# Revit family: Window-Casement-Pella-Architect_Series-Fixed
name_source: partatom
category: Windows
revit_build: Autodesk Revit Architecture 2013 (Build: 20130531_2115(x64)
units: mm (PartAtom-declared; Revit-internal decimal feet)

## types (88) — shared parameters
Analytic Construction = <None>
Architectural Data Sheet = To be determined
Architectural Design Manual = www.pellaadm.com
Construction Type = -
Cross Grille Pattern = No
Custom Grille Pattern = No
Custom Horizontal Lites = 2
Custom Vertical Lites = 3
Default Sill Height = 2' - 7 1/2"
Description = Casement - Fixed Unit
Egress Window = No
Energy Efficiency = http://www.pella.com
Environmental Commitment = http://www.pella.com
Ext Finish = Aluminum - Pella - Brown
Glazing Finish = Glass - Pella - Clear Insulating Glass
Glazing Thickness = 0' - 0 5/8"
Grille Visibility = Yes
Heat Transfer Coefficient (U) = 0.1000 BTU/(h·ft²·°F)
Int Finish = Wood - Pella - Pine
Manufacturer = Pella Windows & Doors
Operation = Fixed
Prairie Grille Pattern = No
Product Documentation Link = http://media.pella.com
Product Name = Architect Series Casement Window
Product Page URL = http://www.pella.com
Series = Architect Series - Aluminum-Clad Wood
Size Constraints = Window Sizing constraints available in 6.35 mm increments
Thermal Resistance (R) = 10.0000 (h·ft²·°F)/BTU
Top Row Grille Pattern = No
Traditional Grille Pattern = Yes
URL = www.pella.com
Wall Closure = By host
zero-valued in all types: Solar Heat Gain Coefficient, Visual Light Transmittance

## per-type parameters (varying)
| type | Head Height | Height | Rough Height | Rough Width | Sash Height | Sash Width | Unit Height | Unit Width | Width |
| 1735 | 5' - 6 1/2" | 2' - 11" | 2' - 11 3/4" | 1' - 5 3/4" | 2' - 8 1/2" | 1' - 2 1/2" | 2' - 11" | 1' - 5" | 1' - 5" |
| 1741 | 6' - 0 1/2" | 3' - 5" | 3' - 5 3/4" | 1' - 5 3/4" | 3' - 2 1/2" | 1' - 2 1/2" | 3' - 5" | 1' - 5" | 1' - 5" |
| 1747 | 6' - 6 1/2" | 3' - 11" | 3' - 11 3/4" | 1' - 5 3/4" | 3' - 8 1/2" | 1' - 2 1/2" | 3' - 11" | 1' - 5" | 1' - 5" |
| 1753 | 7' - 0 1/2" | 4' - 5" | 4' - 5 3/4" | 1' - 5 3/4" | 4' - 2 1/2" | 1' - 2 1/2" | 4' - 5" | 1' - 5" | 1' - 5" |
| 1759 | 7' - 6 1/2" | 4' - 11" | 4' - 11 3/4" | 1' - 5 3/4" | 4' - 8 1/2" | 1' - 2 1/2" | 4' - 11" | 1' - 5" | 1' - 5" |
| 1765 | 8' - 0 1/2" | 5' - 5" | 5' - 5 3/4" | 1' - 5 3/4" | 5' - 2 1/2" | 1' - 2 1/2" | 5' - 5" | 1' - 5" | 1' - 5" |
| 1771 | 8' - 6 1/2" | 5' - 11" | 5' - 11 3/4" | 1' - 5 3/4" | 5' - 8 1/2" | 1' - 2 1/2" | 5' - 11" | 1' - 5" | 1' - 5" |
| 1773 | 8' - 8 1/2" | 6' - 1" | 6' - 1 3/4" | 1' - 5 3/4" | 5' - 10 1/2" | 1' - 2 1/2" | 6' - 1" | 1' - 5" | 1' - 5" |
| 2135 | 5' - 6 1/2" | 2' - 11" | 2' - 11 3/4" | 1' - 9 3/4" | 2' - 8 1/2" | 1' - 6 1/2" | 2' - 11" | 1' - 9" | 1' - 9" |
| 2141 | 6' - 0 1/2" | 3' - 5" | 3' - 5 3/4" | 1' - 9 3/4" | 3' - 2 1/2" | 1' - 6 1/2" | 3' - 5" | 1' - 9" | 1' - 9" |
| 2147 | 6' - 6 1/2" | 3' - 11" | 3' - 11 3/4" | 1' - 9 3/4" | 3' - 8 1/2" | 1' - 6 1/2" | 3' - 11" | 1' - 9" | 1' - 9" |
| 2153 | 7' - 0 1/2" | 4' - 5" | 4' - 5 3/4" | 1' - 9 3/4" | 4' - 2 1/2" | 1' - 6 1/2" | 4' - 5" | 1' - 9" | 1' - 9" |
| 2159 | 7' - 6 1/2" | 4' - 11" | 4' - 11 3/4" | 1' - 9 3/4" | 4' - 8 1/2" | 1' - 6 1/2" | 4' - 11" | 1' - 9" | 1' - 9" |
| 2165 | 8' - 0 1/2" | 5' - 5" | 5' - 5 3/4" | 1' - 9 3/4" | 5' - 2 1/2" | 1' - 6 1/2" | 5' - 5" | 1' - 9" | 1' - 9" |
| 2171 | 8' - 6 1/2" | 5' - 11" | 5' - 11 3/4" | 1' - 9 3/4" | 5' - 8 1/2" | 1' - 6 1/2" | 5' - 11" | 1' - 9" | 1' - 9" |
| 2173 | 8' - 8 1/2" | 6' - 1" | 6' - 1 3/4" | 1' - 9 3/4" | 5' - 10 1/2" | 1' - 6 1/2" | 6' - 1" | 1' - 9" | 1' - 9" |
| 2335 | 5' - 6 1/2" | 2' - 11" | 2' - 11 3/4" | 1' - 11 3/4" | 2' - 8 1/2" | 1' - 8 1/2" | 2' - 11" | 1' - 11" | 1' - 11" |
| 2341 | 6' - 0 1/2" | 3' - 5" | 3' - 5 3/4" | 1' - 11 3/4" | 3' - 2 1/2" | 1' - 8 1/2" | 3' - 5" | 1' - 11" | 1' - 11" |
| 2347 | 6' - 6 1/2" | 3' - 11" | 3' - 11 3/4" | 1' - 11 3/4" | 3' - 8 1/2" | 1' - 8 1/2" | 3' - 11" | 1' - 11" | 1' - 11" |
| 2353 | 7' - 0 1/2" | 4' - 5" | 4' - 5 3/4" | 1' - 11 3/4" | 4' - 2 1/2" | 1' - 8 1/2" | 4' - 5" | 1' - 11" | 1' - 11" |
| 2359 | 7' - 6 1/2" | 4' - 11" | 4' - 11 3/4" | 1' - 11 3/4" | 4' - 8 1/2" | 1' - 8 1/2" | 4' - 11" | 1' - 11" | 1' - 11" |
| 2365 | 8' - 0 1/2" | 5' - 5" | 5' - 5 3/4" | 1' - 11 3/4" | 5' - 2 1/2" | 1' - 8 1/2" | 5' - 5" | 1' - 11" | 1' - 11" |
| 2371 | 8' - 6 1/2" | 5' - 11" | 5' - 11 3/4" | 1' - 11 3/4" | 5' - 8 1/2" | 1' - 8 1/2" | 5' - 11" | 1' - 11" | 1' - 11" |
| 2373 | 8' - 8 1/2" | 6' - 1" | 6' - 1 3/4" | 1' - 11 3/4" | 5' - 10 1/2" | 1' - 8 1/2" | 6' - 1" | 1' - 11" | 1' - 11" |
| 2535 | 5' - 6 1/2" | 2' - 11" | 2' - 11 3/4" | 2' - 1 3/4" | 2' - 8 1/2" | 1' - 10 1/2" | 2' - 11" | 2' - 1" | 2' - 1" |
| 2541 | 6' - 0 1/2" | 3' - 5" | 3' - 5 3/4" | 2' - 1 3/4" | 3' - 2 1/2" | 1' - 10 1/2" | 3' - 5" | 2' - 1" | 2' - 1" |
| 2547 | 6' - 6 1/2" | 3' - 11" | 3' - 11 3/4" | 2' - 1 3/4" | 3' - 8 1/2" | 1' - 10 1/2" | 3' - 11" | 2' - 1" | 2' - 1" |
| 2553 | 7' - 0 1/2" | 4' - 5" | 4' - 5 3/4" | 2' - 1 3/4" | 4' - 2 1/2" | 1' - 10 1/2" | 4' - 5" | 2' - 1" | 2' - 1" |
| 2559 | 7' - 6 1/2" | 4' - 11" | 4' - 11 3/4" | 2' - 1 3/4" | 4' - 8 1/2" | 1' - 10 1/2" | 4' - 11" | 2' - 1" | 2' - 1" |
| 2565 | 8' - 0 1/2" | 5' - 5" | 5' - 5 3/4" | 2' - 1 3/4" | 5' - 2 1/2" | 1' - 10 1/2" | 5' - 5" | 2' - 1" | 2' - 1" |
| 2571 | 8' - 6 1/2" | 5' - 11" | 5' - 11 3/4" | 2' - 1 3/4" | 5' - 8 1/2" | 1' - 10 1/2" | 5' - 11" | 2' - 1" | 2' - 1" |
| 2573 | 8' - 8 1/2" | 6' - 1" | 6' - 1 3/4" | 2' - 1 3/4" | 5' - 10 1/2" | 1' - 10 1/2" | 6' - 1" | 2' - 1" | 2' - 1" |
| 2935 | 5' - 6 1/2" | 2' - 11" | 2' - 11 3/4" | 2' - 5 3/4" | 2' - 8 1/2" | 2' - 2 1/2" | 2' - 11" | 2' - 5" | 2' - 5" |
| 2941 | 6' - 0 1/2" | 3' - 5" | 3' - 5 3/4" | 2' - 5 3/4" | 3' - 2 1/2" | 2' - 2 1/2" | 3' - 5" | 2' - 5" | 2' - 5" |
| 2947 | 6' - 6 1/2" | 3' - 11" | 3' - 11 3/4" | 2' - 5 3/4" | 3' - 8 1/2" | 2' - 2 1/2" | 3' - 11" | 2' - 5" | 2' - 5" |
| 2953 | 7' - 0 1/2" | 4' - 5" | 4' - 5 3/4" | 2' - 5 3/4" | 4' - 2 1/2" | 2' - 2 1/2" | 4' - 5" | 2' - 5" | 2' - 5" |
| 2959 | 7' - 6 1/2" | 4' - 11" | 4' - 11 3/4" | 2' - 5 3/4" | 4' - 8 1/2" | 2' - 2 1/2" | 4' - 11" | 2' - 5" | 2' - 5" |
| 2965 | 8' - 0 1/2" | 5' - 5" | 5' - 5 3/4" | 2' - 5 3/4" | 5' - 2 1/2" | 2' - 2 1/2" | 5' - 5" | 2' - 5" | 2' - 5" |
| 2971 | 8' - 6 1/2" | 5' - 11" | 5' - 11 3/4" | 2' - 5 3/4" | 5' - 8 1/2" | 2' - 2 1/2" | 5' - 11" | 2' - 5" | 2' - 5" |
| 2973 | 8' - 8 1/2" | 6' - 1" | 6' - 1 3/4" | 2' - 5 3/4" | 5' - 10 1/2" | 2' - 2 1/2" | 6' - 1" | 2' - 5" | 2' - 5" |
| 3235 | 5' - 6 1/2" | 2' - 11" | 2' - 11 3/4" | 2' - 8 3/4" | 2' - 8 1/2" | 2' - 5 1/2" | 2' - 11" | 2' - 8" | 2' - 8" |
| 3241 | 6' - 0 1/2" | 3' - 5" | 3' - 5 3/4" | 2' - 8 3/4" | 3' - 2 1/2" | 2' - 5 1/2" | 3' - 5" | 2' - 8" | 2' - 8" |
| 3247 | 6' - 6 1/2" | 3' - 11" | 3' - 11 3/4" | 2' - 8 3/4" | 3' - 8 1/2" | 2' - 5 1/2" | 3' - 11" | 2' - 8" | 2' - 8" |
| 3253 | 7' - 0 1/2" | 4' - 5" | 4' - 5 3/4" | 2' - 8 3/4" | 4' - 2 1/2" | 2' - 5 1/2" | 4' - 5" | 2' - 8" | 2' - 8" |
| 3259 | 7' - 6 1/2" | 4' - 11" | 4' - 11 3/4" | 2' - 8 3/4" | 4' - 8 1/2" | 2' - 5 1/2" | 4' - 11" | 2' - 8" | 2' - 8" |
| 3265 | 8' - 0 1/2" | 5' - 5" | 5' - 5 3/4" | 2' - 8 3/4" | 5' - 2 1/2" | 2' - 5 1/2" | 5' - 5" | 2' - 8" | 2' - 8" |
| 3271 | 8' - 6 1/2" | 5' - 11" | 5' - 11 3/4" | 2' - 8 3/4" | 5' - 8 1/2" | 2' - 5 1/2" | 5' - 11" | 2' - 8" | 2' - 8" |
| 3273 | 8' - 8 1/2" | 6' - 1" | 6' - 1 3/4" | 2' - 8 3/4" | 5' - 10 1/2" | 2' - 5 1/2" | 6' - 1" | 2' - 8" | 2' - 8" |
| 3535 | 5' - 6 1/2" | 2' - 11" | 2' - 11 3/4" | 2' - 11 3/4" | 2' - 8 1/2" | 2' - 8 1/2" | 2' - 11" | 2' - 11" | 2' - 11" |
| 3541 | 6' - 0 1/2" | 3' - 5" | 3' - 5 3/4" | 2' - 11 3/4" | 3' - 2 1/2" | 2' - 8 1/2" | 3' - 5" | 2' - 11" | 2' - 11" |
| 3547 | 6' - 6 1/2" | 3' - 11" | 3' - 11 3/4" | 2' - 11 3/4" | 3' - 8 1/2" | 2' - 8 1/2" | 3' - 11" | 2' - 11" | 2' - 11" |
| 3553 | 7' - 0 1/2" | 4' - 5" | 4' - 5 3/4" | 2' - 11 3/4" | 4' - 2 1/2" | 2' - 8 1/2" | 4' - 5" | 2' - 11" | 2' - 11" |
| 3559 | 7' - 6 1/2" | 4' - 11" | 4' - 11 3/4" | 2' - 11 3/4" | 4' - 8 1/2" | 2' - 8 1/2" | 4' - 11" | 2' - 11" | 2' - 11" |
| 3565 | 8' - 0 1/2" | 5' - 5" | 5' - 5 3/4" | 2' - 11 3/4" | 5' - 2 1/2" | 2' - 8 1/2" | 5' - 5" | 2' - 11" | 2' - 11" |
| 3571 | 8' - 6 1/2" | 5' - 11" | 5' - 11 3/4" | 2' - 11 3/4" | 5' - 8 1/2" | 2' - 8 1/2" | 5' - 11" | 2' - 11" | 2' - 11" |
| 3573 | 8' - 8 1/2" | 6' - 1" | 6' - 1 3/4" | 2' - 11 3/4" | 5' - 10 1/2" | 2' - 8 1/2" | 6' - 1" | 2' - 11" | 2' - 11" |
| 4135 | 5' - 6 1/2" | 2' - 11" | 2' - 11 3/4" | 3' - 5 3/4" | 2' - 8 1/2" | 3' - 2 1/2" | 2' - 11" | 3' - 5" | 3' - 5" |
| 4141 | 6' - 0 1/2" | 3' - 5" | 3' - 5 3/4" | 3' - 5 3/4" | 3' - 2 1/2" | 3' - 2 1/2" | 3' - 5" | 3' - 5" | 3' - 5" |
| 4147 | 6' - 6 1/2" | 3' - 11" | 3' - 11 3/4" | 3' - 5 3/4" | 3' - 8 1/2" | 3' - 2 1/2" | 3' - 11" | 3' - 5" | 3' - 5" |
| 4153 | 7' - 0 1/2" | 4' - 5" | 4' - 5 3/4" | 3' - 5 3/4" | 4' - 2 1/2" | 3' - 2 1/2" | 4' - 5" | 3' - 5" | 3' - 5" |
| 4159 | 7' - 6 1/2" | 4' - 11" | 4' - 11 3/4" | 3' - 5 3/4" | 4' - 8 1/2" | 3' - 2 1/2" | 4' - 11" | 3' - 5" | 3' - 5" |
| 4165 | 8' - 0 1/2" | 5' - 5" | 5' - 5 3/4" | 3' - 5 3/4" | 5' - 2 1/2" | 3' - 2 1/2" | 5' - 5" | 3' - 5" | 3' - 5" |
| 4171 | 8' - 6 1/2" | 5' - 11" | 5' - 11 3/4" | 3' - 5 3/4" | 5' - 8 1/2" | 3' - 2 1/2" | 5' - 11" | 3' - 5" | 3' - 5" |
| 4173 | 8' - 8 1/2" | 6' - 1" | 6' - 1 3/4" | 3' - 5 3/4" | 5' - 10 1/2" | 3' - 2 1/2" | 6' - 1" | 3' - 5" | 3' - 5" |
| 4735 | 5' - 6 1/2" | 2' - 11" | 2' - 11 3/4" | 3' - 11 3/4" | 2' - 8 1/2" | 3' - 8 1/2" | 2' - 11" | 3' - 11" | 3' - 11" |
| 4741 | 6' - 0 1/2" | 3' - 5" | 3' - 5 3/4" | 3' - 11 3/4" | 3' - 2 1/2" | 3' - 8 1/2" | 3' - 5" | 3' - 11" | 3' - 11" |
| 4747 | 6' - 6 1/2" | 3' - 11" | 3' - 11 3/4" | 3' - 11 3/4" | 3' - 8 1/2" | 3' - 8 1/2" | 3' - 11" | 3' - 11" | 3' - 11" |
| 4753 | 7' - 0 1/2" | 4' - 5" | 4' - 5 3/4" | 3' - 11 3/4" | 4' - 2 1/2" | 3' - 8 1/2" | 4' - 5" | 3' - 11" | 3' - 11" |
| 4759 | 7' - 6 1/2" | 4' - 11" | 4' - 11 3/4" | 3' - 11 3/4" | 4' - 8 1/2" | 3' - 8 1/2" | 4' - 11" | 3' - 11" | 3' - 11" |
| 4765 | 8' - 0 1/2" | 5' - 5" | 5' - 5 3/4" | 3' - 11 3/4" | 5' - 2 1/2" | 3' - 8 1/2" | 5' - 5" | 3' - 11" | 3' - 11" |
| 4771 | 8' - 6 1/2" | 5' - 11" | 5' - 11 3/4" | 3' - 11 3/4" | 5' - 8 1/2" | 3' - 8 1/2" | 5' - 11" | 3' - 11" | 3' - 11" |
| 4773 | 8' - 8 1/2" | 6' - 1" | 6' - 1 3/4" | 3' - 11 3/4" | 5' - 10 1/2" | 3' - 8 1/2" | 6' - 1" | 3' - 11" | 3' - 11" |
| 5335 | 5' - 6 1/2" | 2' - 11" | 2' - 11 3/4" | 4' - 5 3/4" | 2' - 8 1/2" | 4' - 2 1/2" | 2' - 11" | 4' - 5" | 4' - 5" |
| 5341 | 6' - 0 1/2" | 3' - 5" | 3' - 5 3/4" | 4' - 5 3/4" | 3' - 2 1/2" | 4' - 2 1/2" | 3' - 5" | 4' - 5" | 4' - 5" |
| 5347 | 6' - 6 1/2" | 3' - 11" | 3' - 11 3/4" | 4' - 5 3/4" | 3' - 8 1/2" | 4' - 2 1/2" | 3' - 11" | 4' - 5" | 4' - 5" |
| 5353 | 7' - 0 1/2" | 4' - 5" | 4' - 5 3/4" | 4' - 5 3/4" | 4' - 2 1/2" | 4' - 2 1/2" | 4' - 5" | 4' - 5" | 4' - 5" |
| 5359 | 7' - 6 1/2" | 4' - 11" | 4' - 11 3/4" | 4' - 5 3/4" | 4' - 8 1/2" | 4' - 2 1/2" | 4' - 11" | 4' - 5" | 4' - 5" |
| 5365 | 8' - 0 1/2" | 5' - 5" | 5' - 5 3/4" | 4' - 5 3/4" | 5' - 2 1/2" | 4' - 2 1/2" | 5' - 5" | 4' - 5" | 4' - 5" |
| 5371 | 8' - 6 1/2" | 5' - 11" | 5' - 11 3/4" | 4' - 5 3/4" | 5' - 8 1/2" | 4' - 2 1/2" | 5' - 11" | 4' - 5" | 4' - 5" |
| 5373 | 8' - 8 1/2" | 6' - 1" | 6' - 1 3/4" | 4' - 5 3/4" | 5' - 10 1/2" | 4' - 2 1/2" | 6' - 1" | 4' - 5" | 4' - 5" |
| 5935 | 5' - 6 1/2" | 2' - 11" | 2' - 11 3/4" | 4' - 11 3/4" | 2' - 8 1/2" | 4' - 8 1/2" | 2' - 11" | 4' - 11" | 4' - 11" |
| 5941 | 6' - 0 1/2" | 3' - 5" | 3' - 5 3/4" | 4' - 11 3/4" | 3' - 2 1/2" | 4' - 8 1/2" | 3' - 5" | 4' - 11" | 4' - 11" |
| 5947 | 6' - 6 1/2" | 3' - 11" | 3' - 11 3/4" | 4' - 11 3/4" | 3' - 8 1/2" | 4' - 8 1/2" | 3' - 11" | 4' - 11" | 4' - 11" |
| 5953 | 7' - 0 1/2" | 4' - 5" | 4' - 5 3/4" | 4' - 11 3/4" | 4' - 2 1/2" | 4' - 8 1/2" | 4' - 5" | 4' - 11" | 4' - 11" |
| 5959 | 7' - 6 1/2" | 4' - 11" | 4' - 11 3/4" | 4' - 11 3/4" | 4' - 8 1/2" | 4' - 8 1/2" | 4' - 11" | 4' - 11" | 4' - 11" |
| 5965 | 8' - 0 1/2" | 5' - 5" | 5' - 5 3/4" | 4' - 11 3/4" | 5' - 2 1/2" | 4' - 8 1/2" | 5' - 5" | 4' - 11" | 4' - 11" |
| 5971 | 8' - 6 1/2" | 5' - 11" | 5' - 11 3/4" | 4' - 11 3/4" | 5' - 8 1/2" | 4' - 8 1/2" | 5' - 11" | 4' - 11" | 4' - 11" |
| 5973 | 8' - 8 1/2" | 6' - 1" | 6' - 1 3/4" | 4' - 11 3/4" | 5' - 10 1/2" | 4' - 8 1/2" | 6' - 1" | 4' - 11" | 4' - 11" |

note: column(s) folded — value = type name in every type: Model

## geometry (parser evidence)
native form markers: Blend x6, Sweep x9
no freeform markers — native parametric forms only
